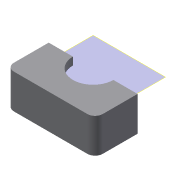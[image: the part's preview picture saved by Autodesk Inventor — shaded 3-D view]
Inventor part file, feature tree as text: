
AUTODESK INVENTOR PART (.ipt)
format: ipt  version: 2022 (Build 260153000, 153)  size: 123,904 bytes
history: native  units: mm
features: extrude x3, sketch x3, projected_geometry x2, other x2, plane x1, fillet x1, reference x1
ambient origin geometry x8: Origin, YZ Plane, XZ Plane, XY Plane, X Axis, Y Axis, Z Axis, Center Point
bodies: Volumenkörper1 (feature_tree)
feature tree (13):
  plane  "Arbeitsebene1"
  extrude  "Extrusion1"  Depth=2.5mm TaperAngle=0.0deg
  extrude  "Extrusion2"  Depth=1.0mm TaperAngle=0.0deg
  extrude  "Extrusion6"  Depth=1.0mm
  fillet  "Rundung2"  Radius=1.0mm
  sketch  "Skizze1"  dims[d2=0.0mm d3=2.5mm d4=0.0mm]
  reference  "Referenz1"
  sketch  "Skizze2"  dims[d5=1.0mm d6=0.0mm d25=1.0mm d26=0.0mm]
  sketch  "Skizze7"  dims[d27=0.0mm d28=1.0mm d29=1.0mm]
  projected_geometry  "Projizierte Kontur2"
  projected_geometry  "Projizierte Kontur3"
  other  "Assembly_Cube_Syringepump_Micro_v3.iam"
  other  "00_Syringe_10ml:1"
